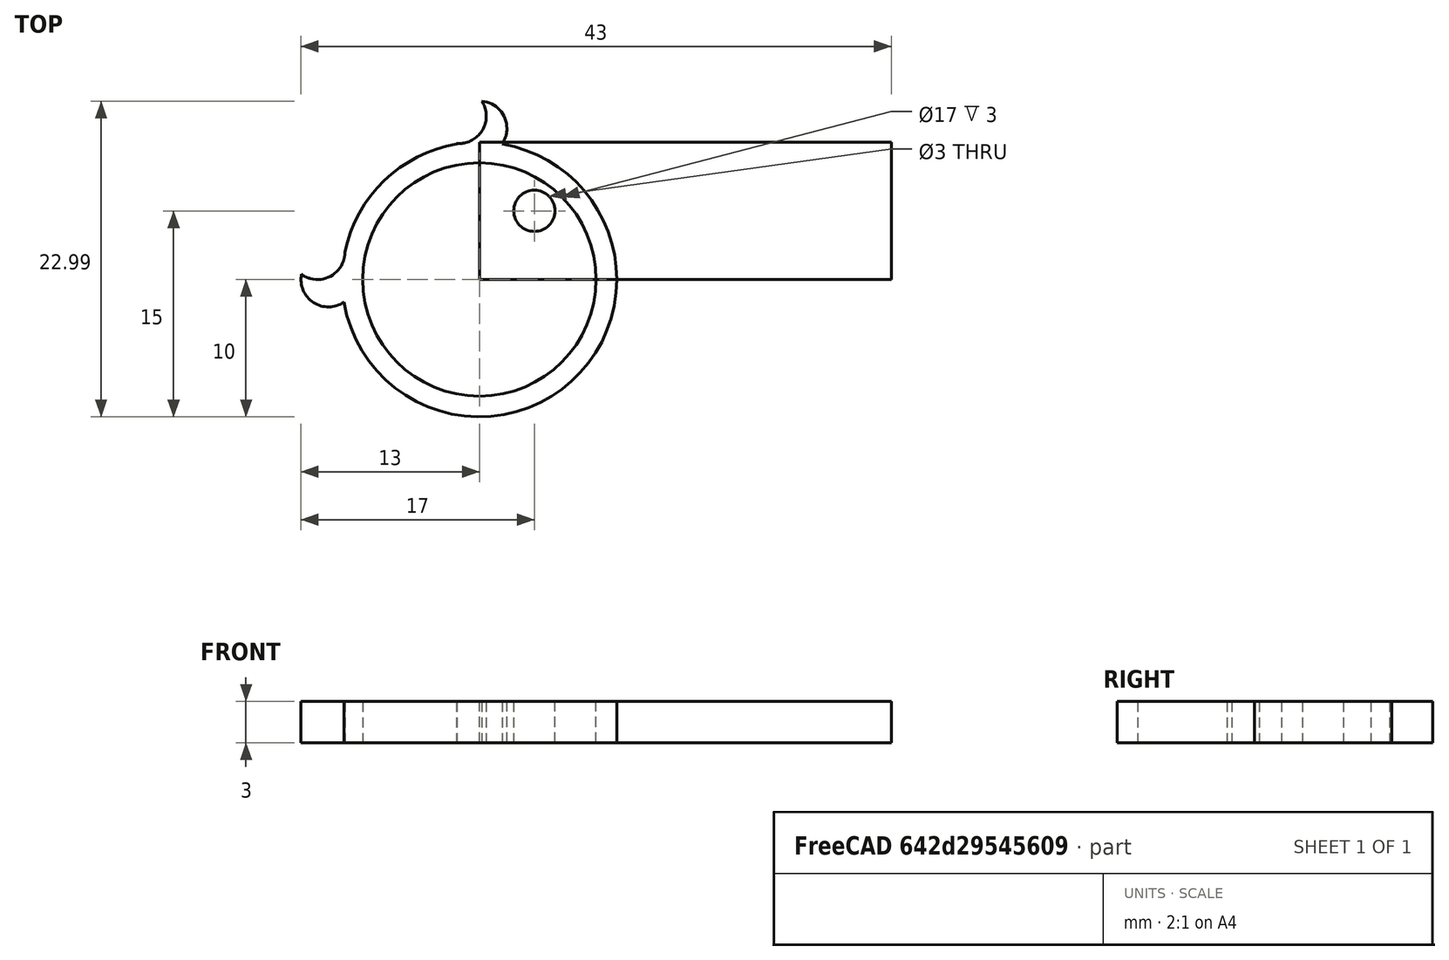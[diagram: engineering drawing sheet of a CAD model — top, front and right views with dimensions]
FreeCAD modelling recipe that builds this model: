
FCSTD DOCUMENT  (FreeCAD 1.0R38806 (Git))
Label: Unnamed2
License: All rights reserved
LicenseURL: https://en.wikipedia.org/wiki/All_rights_reserved
objects: Part::Cylinder×7, Part::Cut×4, Part::Box×1, Part::MultiFuse×1
note: 13 computed .brp shape members not serialized (recipe doc carries the construction recipe); baked Part::Feature solids carry a one-line shape summary decoded from their .brp

FEATURE [Part::Box] Box  label="Cube"
  AttacherType = Attacher::AttachEngine3D
  Height = 3
  Length = 30
  Width = 10
FEATURE [Part::Cylinder] Cylinder
  Angle = 360
  AttacherType = Attacher::AttachEngine3D
  FirstAngle = 0
  Height = 10
  Placement = pos=(4,5,0) rot=(0,0,1;0rad)
  Radius = 1.5
  SecondAngle = 0
FEATURE [Part::Cut] Cut
  Base = -> Box
  Tool = -> Cylinder
FEATURE [Part::Cylinder] Cylinder001
  Angle = 360
  AttacherType = Attacher::AttachEngine3D
  FirstAngle = 0
  Height = 3
  Radius = 10
  SecondAngle = 0
FEATURE [Part::Cylinder] Cylinder002
  Angle = 360
  AttacherType = Attacher::AttachEngine3D
  FirstAngle = 0
  Height = 10
  Radius = 8.5
  SecondAngle = 0
FEATURE [Part::Cut] Cut001
  Base = -> Cylinder001
  Tool = -> Cylinder002
FEATURE [Part::Cylinder] Cylinder003
  Angle = 360
  AttacherType = Attacher::AttachEngine3D
  FirstAngle = 0
  Height = 3
  Placement = pos=(0,11,0) rot=(0,0,1;0rad)
  Radius = 2
  SecondAngle = 0
FEATURE [Part::Cylinder] Cylinder004
  Angle = 360
  AttacherType = Attacher::AttachEngine3D
  FirstAngle = 0
  Height = 3
  Placement = pos=(-11,0,0) rot=(0,0,1;0rad)
  Radius = 2
  SecondAngle = 0
FEATURE [Part::MultiFuse] Fusion  label="Anillo"
  Shapes = -> [Cut001,Cylinder004,Cylinder003]
FEATURE [Part::Cylinder] Cylinder005
  Angle = 360
  AttacherType = Attacher::AttachEngine3D
  FirstAngle = 0
  Height = 3
  Placement = pos=(-1.5,11.9,0) rot=(0,0,-1;1.8326rad)
  Radius = 2
  SecondAngle = 0
FEATURE [Part::Cut] Cut002
  Base = -> Fusion
  Tool = -> Cylinder005
FEATURE [Part::Cylinder] Cylinder006
  Angle = 360
  AttacherType = Attacher::AttachEngine3D
  FirstAngle = 0
  Height = 3
  Placement = pos=(-11.8,2,0) rot=(0,0,-1;1.8326rad)
  Radius = 2
  SecondAngle = 0
FEATURE [Part::Cut] Cut003
  Base = -> Cut002
  Tool = -> Cylinder006
